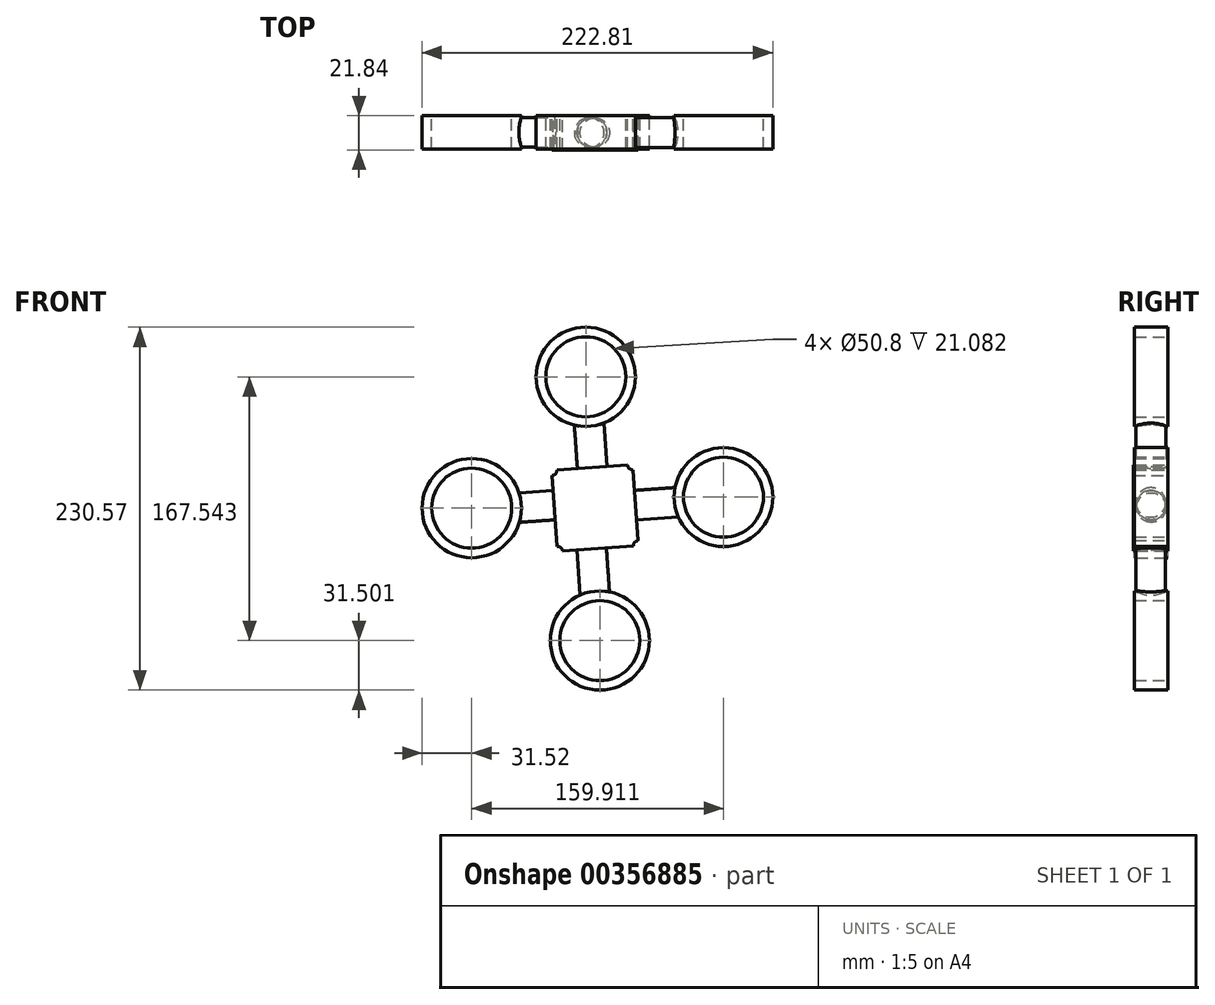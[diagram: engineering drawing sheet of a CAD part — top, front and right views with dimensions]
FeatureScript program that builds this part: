
annotation { "Feature Type Name" : "Feature", "Feature Type Description" : "" }
export const myFeature = defineFeature(function(context is Context, id is Id, definition is map)
    precondition{}
    {
        {
            var Q0;
            Q0=qCreatedBy(makeId("Front.planeOp"),FACE);
            var sketch = newSketch(context, id + "F0", { "sketchPlane" : qUnion([Q0])});
            skCircle(sketch, "E0.cCircle", {"center": v(0, 0) * mm, "radius": 36.4 * mm, "construction": true});
            skLineSegment(sketch, "E0.0", {"start": v(-27.47, 23.87) * mm, "end": v(23.87, 27.47) * mm});
            skLineSegment(sketch, "E0.1", {"start": v(23.87, 27.47) * mm, "end": v(27.47, -23.87) * mm});
            skLineSegment(sketch, "E0.2", {"start": v(27.47, -23.87) * mm, "end": v(-23.87, -27.47) * mm});
            skLineSegment(sketch, "E0.3", {"start": v(-23.87, -27.47) * mm, "end": v(-27.47, 23.87) * mm});
            skSolve(sketch);
        }
        {
            var Q0;
            Q0=makeQuery(id+"F0.imprint","IMPRINT",FACE,{"disambiguationData":[TD([[makeQuery(id+"F0.imprint","IMPRINT",EDGE,{"derivedFrom":sQuery(id+"F0.wireOp",EDGE,"E0.0")}),-1.0]])]});
            extrude(context, id + "F1", {"entities" : qUnion([Q0]), "depth" : 21.84 * mm});
        }
        {
            var Q0;
            Q0=makeQuery(id+"F1.opExtrude","SWEPT_FACE",FACE,{"disambiguationData":[OSD([sQuery(id+"F0.wireOp",EDGE,"E0.0")])]});
            var sketch = newSketch(context, id + "F2", { "sketchPlane" : qUnion([Q0])});
            skCircle(sketch, "E1", {"center": v(0, -10.78) * mm, "radius": 9.46 * mm});
            skSolve(sketch);
        }
        {
            var Q0;
            Q0=makeQuery(id+"F1.opExtrude","SWEPT_FACE",FACE,{"disambiguationData":[OSD([sQuery(id+"F0.wireOp",EDGE,"E0.1")])]});
            var sketch = newSketch(context, id + "F3", { "sketchPlane" : qUnion([Q0])});
            skCircle(sketch, "E2", {"center": v(-10.78, 0) * mm, "radius": 9.46 * mm});
            skSolve(sketch);
        }
        {
            var Q0;
            Q0=makeQuery(id+"F1.opExtrude","SWEPT_FACE",FACE,{"disambiguationData":[OSD([sQuery(id+"F0.wireOp",EDGE,"E0.3")])]});
            var sketch = newSketch(context, id + "F4", { "sketchPlane" : qUnion([Q0])});
            skCircle(sketch, "E3", {"center": v(10.5, 3.7) * mm, "radius": 9.35 * mm});
            skSolve(sketch);
        }
        {
            var Q0;
            Q0=makeQuery(id+"F1.opExtrude","SWEPT_FACE",FACE,{"disambiguationData":[OSD([sQuery(id+"F0.wireOp",EDGE,"E0.2")])]});
            var sketch = newSketch(context, id + "F5", { "sketchPlane" : qUnion([Q0])});
            skCircle(sketch, "E4", {"center": v(-3.96, 10.78) * mm, "radius": 9.36 * mm});
            skSolve(sketch);
        }
        {
            var Q0;
            Q0=makeQuery(id+"F5.imprint","IMPRINT",FACE,{"disambiguationData":[TD([[makeQuery(id+"F5.imprint","IMPRINT",EDGE,{"derivedFrom":sQuery(id+"F5.wireOp",EDGE,"E4")}),1.0]])]});
            extrude(context, id + "F6", {"entities" : qUnion([Q0]), "operationType" : NewBodyOperationType.ADD, "depth" : 58.42 * mm});
        }
        {
            var Q0;
            Q0=makeQuery(id+"F3.imprint","IMPRINT",FACE,{"disambiguationData":[TD([[makeQuery(id+"F3.imprint","IMPRINT",EDGE,{"derivedFrom":sQuery(id+"F3.wireOp",EDGE,"E2")}),1.0]])]});
            extrude(context, id + "F7", {"entities" : qUnion([Q0]), "operationType" : NewBodyOperationType.ADD, "depth" : 55.63 * mm});
        }
        {
            var Q0;
            Q0=makeQuery(id+"F4.imprint","IMPRINT",FACE,{"disambiguationData":[TD([[makeQuery(id+"F4.imprint","IMPRINT",EDGE,{"derivedFrom":sQuery(id+"F4.wireOp",EDGE,"E3")}),1.0]])]});
            extrude(context, id + "F8", {"entities" : qUnion([Q0]), "operationType" : NewBodyOperationType.ADD, "depth" : 52.83 * mm});
        }
        {
            var Q0;
            Q0=makeQuery(id+"F2.imprint","IMPRINT",FACE,{"disambiguationData":[TD([[makeQuery(id+"F2.imprint","IMPRINT",EDGE,{"derivedFrom":sQuery(id+"F2.wireOp",EDGE,"E1")}),1.0]])]});
            extrude(context, id + "F9", {"entities" : qUnion([Q0]), "operationType" : NewBodyOperationType.ADD, "depth" : 58.42 * mm});
        }
        {
            var Q0;
            Q0=qCreatedBy(makeId("Front.planeOp"),FACE);
            var sketch = newSketch(context, id + "F10", { "sketchPlane" : qUnion([Q0])});
            skCircle(sketch, "E5", {"center": v(3.05, -84.13) * mm, "radius": 31.5 * mm});
            skSolve(sketch);
        }
        {
            var Q0;
            Q0=qCreatedBy(makeId("Front.planeOp"),FACE);
            var sketch = newSketch(context, id + "F11", { "sketchPlane" : qUnion([Q0])});
            skCircle(sketch, "E6", {"center": v(-78.38, 0) * mm, "radius": 31.52 * mm});
            skSolve(sketch);
        }
        {
            var Q0;
            Q0=qCreatedBy(makeId("Front.planeOp"),FACE);
            var sketch = newSketch(context, id + "F12", { "sketchPlane" : qUnion([Q0])});
            skCircle(sketch, "E7", {"center": v(81.53, 6.99) * mm, "radius": 31.38 * mm});
            skSolve(sketch);
        }
        {
            var Q0;
            Q0=qCreatedBy(makeId("Front.planeOp"),FACE);
            var sketch = newSketch(context, id + "F13", { "sketchPlane" : qUnion([Q0])});
            skCircle(sketch, "E8", {"center": v(-5.87, 83.41) * mm, "radius": 31.53 * mm});
            skSolve(sketch);
        }
        {
            var Q0;
            Q0=makeQuery(id+"F12.imprint","IMPRINT",FACE,{"disambiguationData":[TD([[makeQuery(id+"F12.imprint","IMPRINT",EDGE,{"derivedFrom":sQuery(id+"F12.wireOp",EDGE,"E7")}),1.0]])]});
            var Q1;
            Q1=makeQuery(id+"F10.imprint","IMPRINT",FACE,{"disambiguationData":[TD([[makeQuery(id+"F10.imprint","IMPRINT",EDGE,{"derivedFrom":sQuery(id+"F10.wireOp",EDGE,"E5")}),1.0]])]});
            var Q2;
            Q2=makeQuery(id+"F11.imprint","IMPRINT",FACE,{"disambiguationData":[TD([[makeQuery(id+"F11.imprint","IMPRINT",EDGE,{"derivedFrom":sQuery(id+"F11.wireOp",EDGE,"E6")}),1.0]])]});
            var Q3;
            Q3=makeQuery(id+"F13.imprint","IMPRINT",FACE,{"disambiguationData":[TD([[makeQuery(id+"F13.imprint","IMPRINT",EDGE,{"derivedFrom":sQuery(id+"F13.wireOp",EDGE,"E8")}),1.0]])]});
            extrude(context, id + "F14", {"entities" : qUnion([Q0, Q1, Q2, Q3]), "operationType" : NewBodyOperationType.ADD, "depth" : 21.08 * mm});
        }
        {
            var Q0;
            Q0=qCreatedBy(makeId("Front.planeOp"),FACE);
            var sketch = newSketch(context, id + "F15", { "sketchPlane" : qUnion([Q0])});
            skCircle(sketch, "E9", {"center": v(-36.38, 0) * mm, "radius": 5.5 * mm});
            skSolve(sketch);
        }
        {
            var Q0;
            Q0=qCreatedBy(makeId("Front.planeOp"),FACE);
            var sketch = newSketch(context, id + "F16", { "sketchPlane" : qUnion([Q0])});
            skCircle(sketch, "E10", {"center": v(38.95, 0) * mm, "radius": 5.73 * mm});
            skSolve(sketch);
        }
        {
            var Q0;
            Q0=qCreatedBy(makeId("Front.planeOp"),FACE);
            var sketch = newSketch(context, id + "F17", { "sketchPlane" : qUnion([Q0])});
            skCircle(sketch, "E11", {"center": v(-4.16, 38.4) * mm, "radius": 5.68 * mm});
            skSolve(sketch);
        }
        {
            var Q0;
            Q0=qCreatedBy(makeId("Front.planeOp"),FACE);
            var sketch = newSketch(context, id + "F18", { "sketchPlane" : qUnion([Q0])});
            skCircle(sketch, "E12", {"center": v(0, -40.4) * mm, "radius": 5.57 * mm});
            skSolve(sketch);
        }
        {
            var Q0;
            Q0=sQuery(id+"F17.wireOp",EDGE,"E11");
            var Q1;
            Q1=sQuery(id+"F16.wireOp",EDGE,"E10");
            var Q2;
            Q2=sQuery(id+"F18.wireOp",EDGE,"E12");
            var Q3;
            Q3=sQuery(id+"F15.wireOp",EDGE,"E9");
            extrude(context, id + "F19", {"bodyType" : ToolBodyType.SURFACE, "surfaceEntities" : qUnion([Q0, Q1, Q2, Q3]), "depth" : 76.45 * mm});
        }
        {
            var Q0;
            Q0=makeQuery(id+"F1.opExtrude","CAP_FACE",FACE,{"disambiguationData":[OSD([sQuery(id+"F0.wireOp",EDGE,"E0.0"),sQuery(id+"F0.wireOp",EDGE,"E0.1"),sQuery(id+"F0.wireOp",EDGE,"E0.2"),sQuery(id+"F0.wireOp",EDGE,"E0.3")])],"isStart":true});
            var sketch = newSketch(context, id + "F20", { "sketchPlane" : qUnion([Q0])});
            skPoint(sketch, "E13", {"position": v(27.47, 23.87) * mm});
            skPoint(sketch, "E14", {"position": v(-23.87, 27.47) * mm});
            skPoint(sketch, "E15", {"position": v(-27.47, -23.87) * mm});
            skPoint(sketch, "E16", {"position": v(23.87, -27.47) * mm});
            skSolve(sketch);
        }
        {
            var Q0;
            Q0=sQuery(id+"F20.wireOp",VERTEX,"E16");
            var Q1;
            Q1=sQuery(id+"F20.wireOp",VERTEX,"E15");
            var Q2;
            Q2=sQuery(id+"F20.wireOp",VERTEX,"E14");
            var Q3;
            Q3=sQuery(id+"F20.wireOp",VERTEX,"E13");
            var Q4;
            Q4=makeQuery(id+"F1.opExtrude","SWEPT_BODY",BODY,{"disambiguationData":[OSD([sQuery(id+"F0.wireOp",EDGE,"E0.0"),sQuery(id+"F0.wireOp",EDGE,"E0.1"),sQuery(id+"F0.wireOp",EDGE,"E0.2"),sQuery(id+"F0.wireOp",EDGE,"E0.3")])]});
            hole(context, id + "F21", {"style" : HoleStyle.SIMPLE, "endStyle" : HoleEndStyle.THROUGH, "holeDiameter" : 6.35 * mm, "isTappedThrough" : true, "tappedDepth" : 12.7 * mm, "tapClearance" : 3, "locations" : qUnion([Q0, Q1, Q2, Q3]), "scope" : qUnion([Q4])});
        }
        {
            var Q0;
            Q0=makeQuery(id+"F14.opExtrude","CAP_FACE",FACE,{"disambiguationData":[OSD([sQuery(id+"F13.wireOp",EDGE,"E8")])],"isStart":true});
            var sketch = newSketch(context, id + "F22", { "sketchPlane" : qUnion([Q0])});
            skCircle(sketch, "E17.cCircle", {"center": v(5.87, 83.41) * mm, "radius": 24.45 * mm, "construction": true});
            skLineSegment(sketch, "E17.0", {"start": v(-20.75, 88.64) * mm, "end": v(-6.64, 107.49) * mm});
            skLineSegment(sketch, "E17.1", {"start": v(-6.64, 107.49) * mm, "end": v(16.9, 108.2) * mm});
            skLineSegment(sketch, "E17.2", {"start": v(16.9, 108.2) * mm, "end": v(32.13, 90.26) * mm});
            skLineSegment(sketch, "E17.3", {"start": v(32.13, 90.26) * mm, "end": v(27.6, 67.15) * mm});
            skLineSegment(sketch, "E17.4", {"start": v(27.6, 67.15) * mm, "end": v(6.7, 56.3) * mm});
            skLineSegment(sketch, "E17.5", {"start": v(6.7, 56.3) * mm, "end": v(-14.82, 65.86) * mm});
            skLineSegment(sketch, "E17.6", {"start": v(-14.82, 65.86) * mm, "end": v(-20.75, 88.64) * mm});
            skPoint(sketch, "E17.0.midPoint", {"position": v(-13.7, 98.07) * mm});
            skSolve(sketch);
        }
        {
            var Q0;
            Q0=sQuery(id+"F22.wireOp",VERTEX,"E17.cCircle.center");
            var Q1;
            Q1=makeQuery(id+"F1.opExtrude","SWEPT_BODY",BODY,{"disambiguationData":[OSD([sQuery(id+"F0.wireOp",EDGE,"E0.0"),sQuery(id+"F0.wireOp",EDGE,"E0.1"),sQuery(id+"F0.wireOp",EDGE,"E0.2"),sQuery(id+"F0.wireOp",EDGE,"E0.3")])]});
            hole(context, id + "F23", {"style" : HoleStyle.SIMPLE, "endStyle" : HoleEndStyle.THROUGH, "holeDiameter" : 50.8 * mm, "isTappedThrough" : true, "tappedDepth" : 12.7 * mm, "tapClearance" : 3, "locations" : qUnion([Q0]), "scope" : qUnion([Q1])});
        }
        {
            var Q0;
            Q0=makeQuery(id+"F14.opExtrude","CAP_FACE",FACE,{"disambiguationData":[OSD([sQuery(id+"F12.wireOp",EDGE,"E7")])],"isStart":true});
            var sketch = newSketch(context, id + "F24", { "sketchPlane" : qUnion([Q0])});
            skCircle(sketch, "E18.cCircle", {"center": v(-81.53, 6.99) * mm, "radius": 23.65 * mm, "construction": true});
            skLineSegment(sketch, "E18.0", {"start": v(-105.27, 18.17) * mm, "end": v(-87.59, 32.52) * mm});
            skLineSegment(sketch, "E18.1", {"start": v(-87.59, 32.52) * mm, "end": v(-65.34, 27.64) * mm});
            skLineSegment(sketch, "E18.2", {"start": v(-65.34, 27.64) * mm, "end": v(-55.29, 7.21) * mm});
            skLineSegment(sketch, "E18.3", {"start": v(-55.29, 7.21) * mm, "end": v(-65, -13.4) * mm});
            skLineSegment(sketch, "E18.4", {"start": v(-65, -13.4) * mm, "end": v(-87.15, -18.65) * mm});
            skLineSegment(sketch, "E18.5", {"start": v(-87.15, -18.65) * mm, "end": v(-105.08, -4.6) * mm});
            skLineSegment(sketch, "E18.6", {"start": v(-105.08, -4.6) * mm, "end": v(-105.27, 18.17) * mm});
            skPoint(sketch, "E18.0.midPoint", {"position": v(-96.43, 25.35) * mm});
            skSolve(sketch);
        }
        {
            var Q0;
            Q0=sQuery(id+"F24.wireOp",VERTEX,"E18.cCircle.center");
            var Q1;
            Q1=makeQuery(id+"F1.opExtrude","SWEPT_BODY",BODY,{"disambiguationData":[OSD([sQuery(id+"F0.wireOp",EDGE,"E0.0"),sQuery(id+"F0.wireOp",EDGE,"E0.1"),sQuery(id+"F0.wireOp",EDGE,"E0.2"),sQuery(id+"F0.wireOp",EDGE,"E0.3")])]});
            hole(context, id + "F25", {"style" : HoleStyle.SIMPLE, "endStyle" : HoleEndStyle.THROUGH, "holeDiameter" : 50.8 * mm, "isTappedThrough" : true, "tappedDepth" : 12.7 * mm, "tapClearance" : 3, "locations" : qUnion([Q0]), "scope" : qUnion([Q1])});
        }
        {
            var Q0;
            Q0=makeQuery(id+"F14.opExtrude","CAP_FACE",FACE,{"disambiguationData":[OSD([sQuery(id+"F11.wireOp",EDGE,"E6")])],"isStart":true});
            var sketch = newSketch(context, id + "F26", { "sketchPlane" : qUnion([Q0])});
            skCircle(sketch, "E19.cCircle", {"center": v(78.38, 0) * mm, "radius": 23.11 * mm, "construction": true});
            skLineSegment(sketch, "E19.0", {"start": v(55.17, 10.93) * mm, "end": v(72.45, 24.96) * mm});
            skLineSegment(sketch, "E19.1", {"start": v(72.45, 24.96) * mm, "end": v(94.2, 20.2) * mm});
            skLineSegment(sketch, "E19.2", {"start": v(94.2, 20.2) * mm, "end": v(104.03, 0.22) * mm});
            skLineSegment(sketch, "E19.3", {"start": v(104.03, 0.22) * mm, "end": v(94.55, -19.92) * mm});
            skLineSegment(sketch, "E19.4", {"start": v(94.55, -19.92) * mm, "end": v(72.9, -25.06) * mm});
            skLineSegment(sketch, "E19.5", {"start": v(72.9, -25.06) * mm, "end": v(55.37, -11.33) * mm});
            skLineSegment(sketch, "E19.6", {"start": v(55.37, -11.33) * mm, "end": v(55.17, 10.93) * mm});
            skPoint(sketch, "E19.0.midPoint", {"position": v(63.81, 17.94) * mm});
            skSolve(sketch);
        }
        {
            var Q0;
            Q0=sQuery(id+"F26.wireOp",VERTEX,"E19.cCircle.center");
            var Q1;
            Q1=makeQuery(id+"F1.opExtrude","SWEPT_BODY",BODY,{"disambiguationData":[OSD([sQuery(id+"F0.wireOp",EDGE,"E0.0"),sQuery(id+"F0.wireOp",EDGE,"E0.1"),sQuery(id+"F0.wireOp",EDGE,"E0.2"),sQuery(id+"F0.wireOp",EDGE,"E0.3")])]});
            hole(context, id + "F27", {"style" : HoleStyle.SIMPLE, "endStyle" : HoleEndStyle.THROUGH, "holeDiameter" : 50.8 * mm, "isTappedThrough" : true, "tappedDepth" : 12.7 * mm, "tapClearance" : 3, "locations" : qUnion([Q0]), "scope" : qUnion([Q1])});
        }
        {
            var Q0;
            Q0=makeQuery(id+"F14.opExtrude","CAP_FACE",FACE,{"disambiguationData":[OSD([sQuery(id+"F10.wireOp",EDGE,"E5")])],"isStart":true});
            var sketch = newSketch(context, id + "F28", { "sketchPlane" : qUnion([Q0])});
            skCircle(sketch, "E20.cCircle", {"center": v(-3.05, -84.13) * mm, "radius": 23.8 * mm, "construction": true});
            skLineSegment(sketch, "E20.0", {"start": v(-30.19, -79.82) * mm, "end": v(-12.88, -58.47) * mm});
            skLineSegment(sketch, "E20.1", {"start": v(-12.88, -58.47) * mm, "end": v(14.25, -62.79) * mm});
            skLineSegment(sketch, "E20.2", {"start": v(14.25, -62.79) * mm, "end": v(24.08, -88.44) * mm});
            skLineSegment(sketch, "E20.3", {"start": v(24.08, -88.44) * mm, "end": v(6.78, -109.78) * mm});
            skLineSegment(sketch, "E20.4", {"start": v(6.78, -109.78) * mm, "end": v(-20.35, -105.47) * mm});
            skLineSegment(sketch, "E20.5", {"start": v(-20.35, -105.47) * mm, "end": v(-30.19, -79.82) * mm});
            skPoint(sketch, "E20.0.midPoint", {"position": v(-21.53, -69.15) * mm});
            skSolve(sketch);
        }
        {
            var Q0;
            Q0=sQuery(id+"F28.wireOp",VERTEX,"E20.cCircle.center");
            var Q1;
            Q1=makeQuery(id+"F1.opExtrude","SWEPT_BODY",BODY,{"disambiguationData":[OSD([sQuery(id+"F0.wireOp",EDGE,"E0.0"),sQuery(id+"F0.wireOp",EDGE,"E0.1"),sQuery(id+"F0.wireOp",EDGE,"E0.2"),sQuery(id+"F0.wireOp",EDGE,"E0.3")])]});
            hole(context, id + "F29", {"style" : HoleStyle.SIMPLE, "endStyle" : HoleEndStyle.THROUGH, "holeDiameter" : 50.8 * mm, "isTappedThrough" : true, "tappedDepth" : 12.7 * mm, "tapClearance" : 3, "locations" : qUnion([Q0]), "scope" : qUnion([Q1])});
        }
    });
